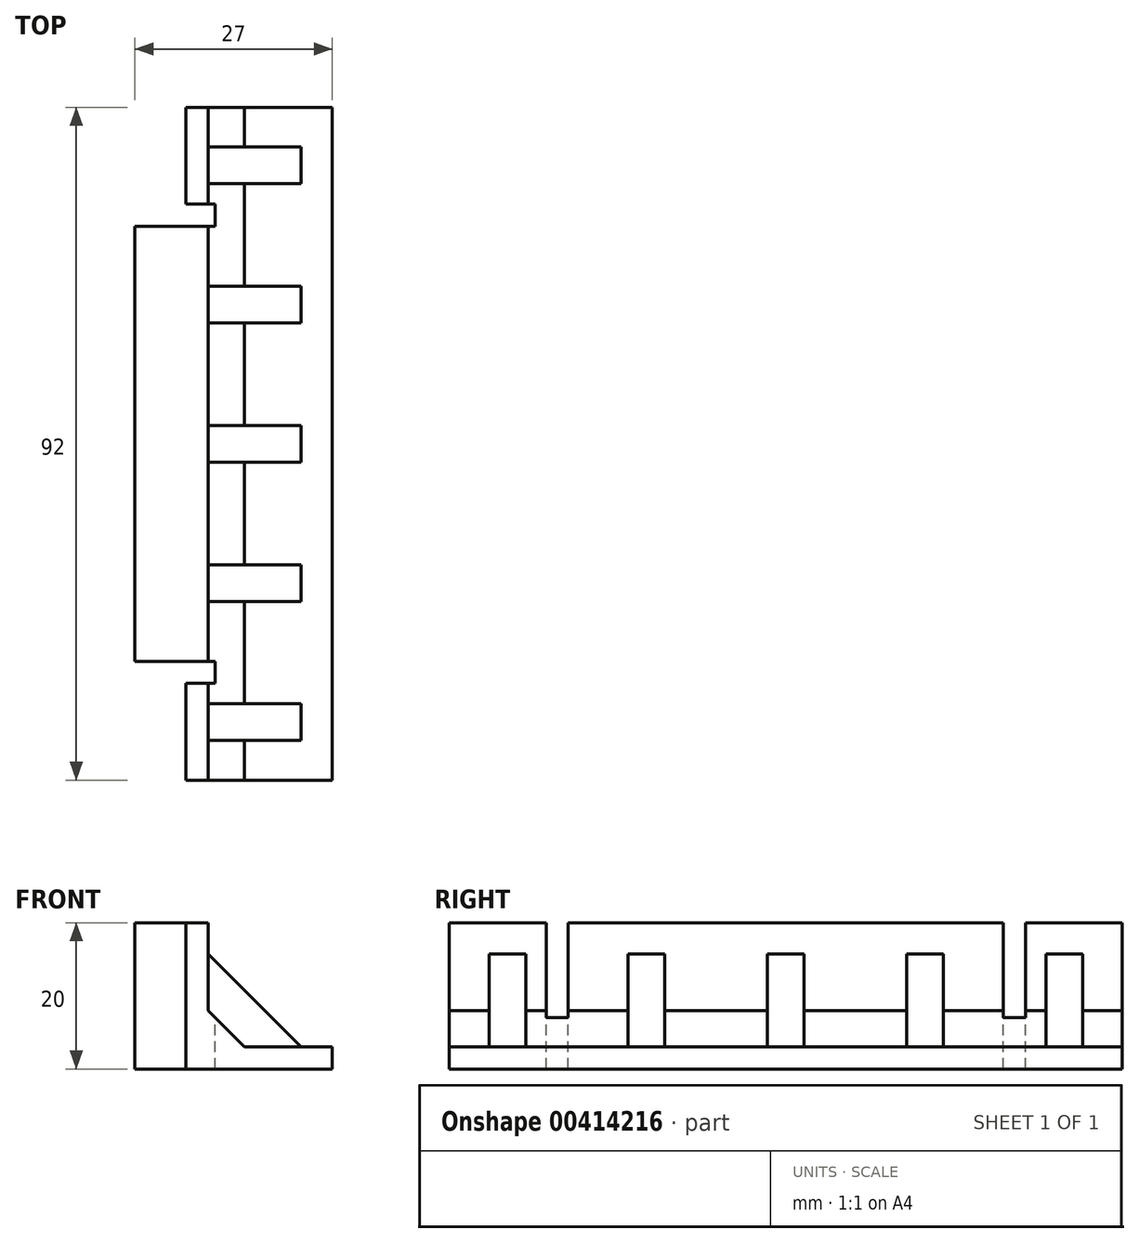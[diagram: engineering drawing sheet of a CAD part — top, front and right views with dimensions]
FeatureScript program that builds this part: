
annotation { "Feature Type Name" : "Feature", "Feature Type Description" : "" }
export const myFeature = defineFeature(function(context is Context, id is Id, definition is map)
    precondition{}
    {
        {
            var Q0;
            Q0=qCreatedBy(makeId("Front.planeOp"),FACE);
            var sketch = newSketch(context, id + "F0", { "sketchPlane" : qUnion([Q0])});
            skLineSegment(sketch, "E0", {"start": v(0, 0) * mm, "end": v(0, 20) * mm});
            skLineSegment(sketch, "E1", {"start": v(0, 20) * mm, "end": v(3, 20) * mm});
            skLineSegment(sketch, "E2", {"start": v(3, 20) * mm, "end": v(3, 3) * mm});
            skLineSegment(sketch, "E3", {"start": v(3, 3) * mm, "end": v(20, 3) * mm});
            skLineSegment(sketch, "E4", {"start": v(20, 3) * mm, "end": v(20, 0) * mm});
            skLineSegment(sketch, "E5", {"start": v(20, 0) * mm, "end": v(0, 0) * mm});
            skSolve(sketch);
        }
        {
            var Q0;
            Q0 = qSketchRegion(id + "F0", true);
            extrude(context, id + "F1", {"entities" : qUnion([Q0]), "endBound" : BoundingType.SYMMETRIC, "oppositeDirection" : true, "depth" : 92 * mm});
        }
        {
            var Q0;
            Q0=makeQuery(id+"F1.opExtrude","SWEPT_EDGE",EDGE,{"disambiguationData":[OSD([sQuery(id+"F0.wireOp",EDGE,"E2"),sQuery(id+"F0.wireOp",EDGE,"E3")])]});
            chamfer(context, id + "F2", {"entities" : qUnion([Q0]), "width" : 5 * mm, "tangentPropagation" : true});
        }
        {
            var Q0;
            Q0=qCreatedBy(makeId("Front.planeOp"),FACE);
            cPlane(context, id + "F3", {"entities" : qUnion([Q0]), "cplaneType" : CPlaneType.OFFSET, "offset" : 19.05 * mm, "width" : 152.4 * mm, "height" : 152.4 * mm});
        }
        {
            var Q0;
            Q0=qCreatedBy(makeId("Front.planeOp"),FACE);
            cPlane(context, id + "F4", {"entities" : qUnion([Q0]), "cplaneType" : CPlaneType.OFFSET, "offset" : 19.05 * mm, "oppositeDirection" : true, "width" : 152.4 * mm, "height" : 152.4 * mm});
        }
        {
            var Q0;
            Q0=qCreatedBy(makeId("Front.planeOp"),FACE);
            var sketch = newSketch(context, id + "F5", { "sketchPlane" : qUnion([Q0])});
            skLineSegment(sketch, "E6", {"start": v(3, 15.7) * mm, "end": v(15.7, 3) * mm});
            skLineSegment(sketch, "E7", {"start": v(15.7, 3) * mm, "end": v(3, 3) * mm});
            skLineSegment(sketch, "E8", {"start": v(3, 3) * mm, "end": v(3, 15.7) * mm});
            skSolve(sketch);
        }
        {
            var Q0;
            Q0 = qSketchRegion(id + "F5", true);
            extrude(context, id + "F6", {"entities" : qUnion([Q0]), "operationType" : NewBodyOperationType.ADD, "endBound" : BoundingType.SYMMETRIC, "depth" : 5 * mm});
        }
        {
            var Q0;
            Q0=qCreatedBy(id+"F3.planeOp",FACE);
            var sketch = newSketch(context, id + "F7", { "sketchPlane" : qUnion([Q0])});
            skLineSegment(sketch, "E9", {"start": v(3, 15.7) * mm, "end": v(15.7, 3) * mm});
            skLineSegment(sketch, "E10", {"start": v(15.7, 3) * mm, "end": v(3, 3) * mm});
            skLineSegment(sketch, "E11", {"start": v(3, 3) * mm, "end": v(3, 15.7) * mm});
            skSolve(sketch);
        }
        {
            var Q0;
            Q0 = qSketchRegion(id + "F7", true);
            extrude(context, id + "F8", {"entities" : qUnion([Q0]), "operationType" : NewBodyOperationType.ADD, "endBound" : BoundingType.SYMMETRIC, "depth" : 5 * mm});
        }
        {
            var Q0;
            Q0=qCreatedBy(id+"F4.planeOp",FACE);
            var sketch = newSketch(context, id + "F9", { "sketchPlane" : qUnion([Q0])});
            skLineSegment(sketch, "E12", {"start": v(3, 15.7) * mm, "end": v(15.7, 3) * mm});
            skLineSegment(sketch, "E13", {"start": v(15.7, 3) * mm, "end": v(3, 3) * mm});
            skLineSegment(sketch, "E14", {"start": v(3, 3) * mm, "end": v(3, 15.7) * mm});
            skSolve(sketch);
        }
        {
            var Q0;
            Q0 = qSketchRegion(id + "F9", true);
            extrude(context, id + "F10", {"entities" : qUnion([Q0]), "operationType" : NewBodyOperationType.ADD, "endBound" : BoundingType.SYMMETRIC, "depth" : 5 * mm});
        }
        {
            var Q0;
            Q0=makeQuery(id+"F1.opExtrude","SWEPT_FACE",FACE,{"disambiguationData":[OSD([sQuery(id+"F0.wireOp",EDGE,"E1")])]});
            var sketch = newSketch(context, id + "F11", { "sketchPlane" : qUnion([Q0])});
            skLineSegment(sketch, "E15.bottom", {"start": v(0, 32.75) * mm, "end": v(4, 32.75) * mm});
            skLineSegment(sketch, "E15.top", {"start": v(0, 29.75) * mm, "end": v(4, 29.75) * mm});
            skLineSegment(sketch, "E15.left", {"start": v(0, 32.75) * mm, "end": v(0, 29.75) * mm});
            skLineSegment(sketch, "E15.right", {"start": v(4, 32.75) * mm, "end": v(4, 29.75) * mm});
            skLineSegment(sketch, "E16.bottom", {"start": v(0, -29.75) * mm, "end": v(4, -29.75) * mm});
            skLineSegment(sketch, "E16.top", {"start": v(0, -32.75) * mm, "end": v(4, -32.75) * mm});
            skLineSegment(sketch, "E16.left", {"start": v(0, -29.75) * mm, "end": v(0, -32.75) * mm});
            skLineSegment(sketch, "E16.right", {"start": v(4, -29.75) * mm, "end": v(4, -32.75) * mm});
            skSolve(sketch);
        }
        {
            var Q0;
            Q0 = qSketchRegion(id + "F11", true);
            extrude(context, id + "F12", {"entities" : qUnion([Q0]), "operationType" : NewBodyOperationType.REMOVE, "endBound" : BoundingType.THROUGH_ALL, "oppositeDirection" : true, "depth" : 25.4 * mm});
        }
        {
            var Q0;
            Q0=qCreatedBy(makeId("Front.planeOp"),FACE);
            cPlane(context, id + "F13", {"entities" : qUnion([Q0]), "cplaneType" : CPlaneType.OFFSET, "offset" : 35.56 * mm, "width" : 152.4 * mm, "height" : 152.4 * mm});
        }
        {
            var Q0;
            Q0=qCreatedBy(id+"F13.planeOp",FACE);
            var sketch = newSketch(context, id + "F14", { "sketchPlane" : qUnion([Q0])});
            skLineSegment(sketch, "E17", {"start": v(15.7, 3) * mm, "end": v(3, 15.7) * mm});
            skLineSegment(sketch, "E18.0", {"start": v(3, 15.7) * mm, "end": v(15.7, 3) * mm});
            skLineSegment(sketch, "E19.0", {"start": v(3, 20) * mm, "end": v(3, 8) * mm});
            skLineSegment(sketch, "E20.0", {"start": v(8, 3) * mm, "end": v(3, 8) * mm});
            skLineSegment(sketch, "E21.0", {"start": v(8, 3) * mm, "end": v(20, 3) * mm});
            skSolve(sketch);
        }
        {
            var Q0;
            Q0 = qSketchRegion(id + "F14", true);
            extrude(context, id + "F15", {"entities" : qUnion([Q0]), "operationType" : NewBodyOperationType.ADD, "depth" : 5 * mm});
        }
        {
            var Q0;
            Q0=qCreatedBy(makeId("Front.planeOp"),FACE);
            cPlane(context, id + "F16", {"entities" : qUnion([Q0]), "cplaneType" : CPlaneType.OFFSET, "offset" : 35.56 * mm, "oppositeDirection" : true, "width" : 152.4 * mm, "height" : 152.4 * mm});
        }
        {
            var Q0;
            Q0=qCreatedBy(id+"F16.planeOp",FACE);
            var sketch = newSketch(context, id + "F17", { "sketchPlane" : qUnion([Q0])});
            skLineSegment(sketch, "E22", {"start": v(3, 15.7) * mm, "end": v(15.7, 3) * mm});
            skLineSegment(sketch, "E23.0", {"start": v(3, 20) * mm, "end": v(3, 8) * mm});
            skLineSegment(sketch, "E24.0.0", {"start": v(15.7, 3) * mm, "end": v(8, 3) * mm});
            skLineSegment(sketch, "E24.0.1", {"start": v(8, 3) * mm, "end": v(3, 8) * mm});
            skLineSegment(sketch, "E24.0.2", {"start": v(3, 8) * mm, "end": v(3, 15.7) * mm});
            skSolve(sketch);
        }
        {
            var Q0;
            Q0 = qSketchRegion(id + "F17", true);
            extrude(context, id + "F18", {"entities" : qUnion([Q0]), "operationType" : NewBodyOperationType.ADD, "oppositeDirection" : true, "depth" : 5 * mm});
        }
        {
            var Q0;
            Q0=makeQuery(id+"F12.boolean.opBoolean","SPLIT",FACE,{"disambiguationData":[TD([makeQuery(id+"F12.opExtrude","SWEPT_FACE",FACE,{"disambiguationData":[OSD([sQuery(id+"F11.wireOp",EDGE,"E15.top")])]})])],"derivedFrom":makeQuery(id+"F1.opExtrude","SWEPT_FACE",FACE,{"disambiguationData":[OSD([sQuery(id+"F0.wireOp",EDGE,"E0")])]})});
            var sketch = newSketch(context, id + "F19", { "sketchPlane" : qUnion([Q0])});
            skLineSegment(sketch, "E25.0.0", {"start": v(-29.75, 0) * mm, "end": v(29.75, 0) * mm});
            skLineSegment(sketch, "E25.0.1", {"start": v(29.75, 0) * mm, "end": v(29.75, 20) * mm});
            skLineSegment(sketch, "E25.0.2", {"start": v(29.75, 20) * mm, "end": v(-29.75, 20) * mm});
            skLineSegment(sketch, "E25.0.3", {"start": v(-29.75, 20) * mm, "end": v(-29.75, 0) * mm});
            skSolve(sketch);
        }
        {
            var Q0;
            Q0 = qSketchRegion(id + "F19", true);
            extrude(context, id + "F20", {"entities" : qUnion([Q0]), "operationType" : NewBodyOperationType.ADD, "depth" : 7 * mm});
        }
    });
